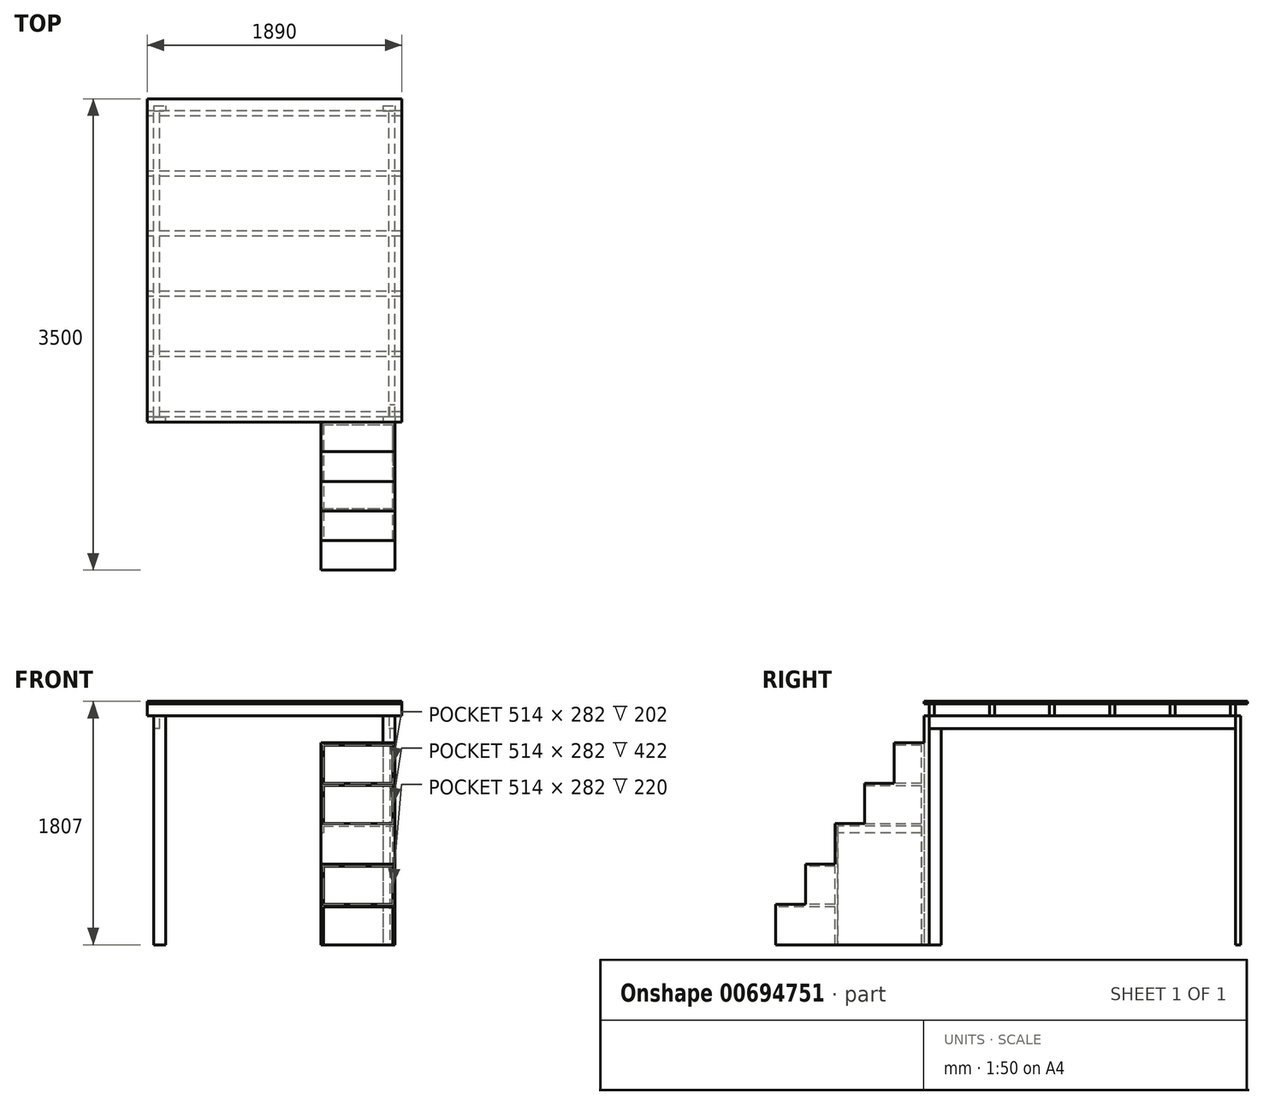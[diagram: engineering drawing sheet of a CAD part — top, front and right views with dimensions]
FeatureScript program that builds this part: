
annotation { "Feature Type Name" : "Feature", "Feature Type Description" : "" }
export const myFeature = defineFeature(function(context is Context, id is Id, definition is map)
    precondition{}
    {
        {
            var Q0;
            Q0=qCreatedBy(makeId("Top.planeOp"),FACE);
            var sketch = newSketch(context, id + "F0", { "sketchPlane" : qUnion([Q0])});
            skLineSegment(sketch, "E0.bottom", {"start": v(-895, 2350) * mm, "end": v(-806, 2350) * mm});
            skLineSegment(sketch, "E0.top", {"start": v(-895, 2312) * mm, "end": v(-806, 2312) * mm});
            skLineSegment(sketch, "E0.left", {"start": v(-895, 2350) * mm, "end": v(-895, 2312) * mm});
            skLineSegment(sketch, "E0.right", {"start": v(-806, 2350) * mm, "end": v(-806, 2312) * mm});
            skLineSegment(sketch, "E1.bottom", {"start": v(-895, 2312) * mm, "end": v(-857, 2312) * mm});
            skLineSegment(sketch, "E1.top", {"start": v(-895, 2223) * mm, "end": v(-857, 2223) * mm});
            skLineSegment(sketch, "E1.left", {"start": v(-895, 2312) * mm, "end": v(-895, 2223) * mm});
            skLineSegment(sketch, "E1.right", {"start": v(-857, 2312) * mm, "end": v(-857, 2223) * mm});
            skLineSegment(sketch, "E2.bottom", {"start": v(806, 2350) * mm, "end": v(895, 2350) * mm});
            skLineSegment(sketch, "E2.top", {"start": v(806, 2312) * mm, "end": v(895, 2312) * mm});
            skLineSegment(sketch, "E2.left", {"start": v(806, 2350) * mm, "end": v(806, 2312) * mm});
            skLineSegment(sketch, "E2.right", {"start": v(895, 2350) * mm, "end": v(895, 2312) * mm});
            skLineSegment(sketch, "E3.bottom", {"start": v(895, 2312) * mm, "end": v(857, 2312) * mm});
            skLineSegment(sketch, "E3.top", {"start": v(895, 2223) * mm, "end": v(857, 2223) * mm});
            skLineSegment(sketch, "E3.left", {"start": v(895, 2312) * mm, "end": v(895, 2223) * mm});
            skLineSegment(sketch, "E3.right", {"start": v(857, 2312) * mm, "end": v(857, 2223) * mm});
            skLineSegment(sketch, "E4.bottom", {"start": v(895, 38) * mm, "end": v(857, 38) * mm});
            skLineSegment(sketch, "E4.top", {"start": v(895, 127) * mm, "end": v(857, 127) * mm});
            skLineSegment(sketch, "E4.left", {"start": v(895, 38) * mm, "end": v(895, 127) * mm});
            skLineSegment(sketch, "E4.right", {"start": v(857, 38) * mm, "end": v(857, 127) * mm});
            skLineSegment(sketch, "E5.bottom", {"start": v(895, 38) * mm, "end": v(806, 38) * mm});
            skLineSegment(sketch, "E5.top", {"start": v(895, 0) * mm, "end": v(806, 0) * mm});
            skLineSegment(sketch, "E5.left", {"start": v(895, 38) * mm, "end": v(895, 0) * mm});
            skLineSegment(sketch, "E5.right", {"start": v(806, 38) * mm, "end": v(806, 0) * mm});
            skLineSegment(sketch, "E6.bottom", {"start": v(-895, 0) * mm, "end": v(-806, 0) * mm});
            skLineSegment(sketch, "E6.top", {"start": v(-895, 38) * mm, "end": v(-806, 38) * mm});
            skLineSegment(sketch, "E6.left", {"start": v(-895, 0) * mm, "end": v(-895, 38) * mm});
            skLineSegment(sketch, "E6.right", {"start": v(-806, 0) * mm, "end": v(-806, 38) * mm});
            skLineSegment(sketch, "E7.bottom", {"start": v(-895, 38) * mm, "end": v(-857, 38) * mm});
            skLineSegment(sketch, "E7.top", {"start": v(-895, 127) * mm, "end": v(-857, 127) * mm});
            skLineSegment(sketch, "E7.left", {"start": v(-895, 38) * mm, "end": v(-895, 127) * mm});
            skLineSegment(sketch, "E7.right", {"start": v(-857, 38) * mm, "end": v(-857, 127) * mm});
            skLineSegment(sketch, "E8", {"start": v(-806, 2350) * mm, "end": v(806, 2350) * mm, "construction": true});
            skLineSegment(sketch, "E9", {"start": v(895, 2223) * mm, "end": v(895, 127) * mm, "construction": true});
            skLineSegment(sketch, "E10", {"start": v(806, 0) * mm, "end": v(-806, 0) * mm, "construction": true});
            skLineSegment(sketch, "E11", {"start": v(-895, 127) * mm, "end": v(-895, 2223) * mm, "construction": true});
            skSolve(sketch);
        }
        {
            var Q0;
            Q0=makeQuery(id+"F0.imprint","IMPRINT",FACE,{"disambiguationData":[TD([[makeQuery(id+"F0.imprint","IMPRINT",EDGE,{"derivedFrom":sQuery(id+"F0.wireOp",EDGE,"E0.bottom")}),-1.0]])]});
            var Q1;
            Q1=makeQuery(id+"F0.imprint","IMPRINT",FACE,{"disambiguationData":[TD([[makeQuery(id+"F0.imprint","IMPRINT",EDGE,{"derivedFrom":sQuery(id+"F0.wireOp",EDGE,"E2.bottom")}),-1.0]])]});
            var Q2;
            Q2=makeQuery(id+"F0.imprint","IMPRINT",FACE,{"disambiguationData":[TD([[makeQuery(id+"F0.imprint","IMPRINT",EDGE,{"derivedFrom":sQuery(id+"F0.wireOp",EDGE,"E5.top")}),-1.0]])]});
            var Q3;
            Q3=makeQuery(id+"F0.imprint","IMPRINT",FACE,{"disambiguationData":[TD([[makeQuery(id+"F0.imprint","IMPRINT",EDGE,{"derivedFrom":sQuery(id+"F0.wireOp",EDGE,"E6.bottom")}),1.0]])]});
            extrude(context, id + "F1", {"entities" : qUnion([Q0, Q1, Q2, Q3]), "depth" : 1700 * mm, "offsetDistance" : 25 * mm});
        }
        {
            var Q0;
            Q0=makeQuery(id+"F0.imprint","IMPRINT",FACE,{"disambiguationData":[TD([[makeQuery(id+"F0.imprint","IMPRINT",EDGE,{"derivedFrom":sQuery(id+"F0.wireOp",EDGE,"E1.bottom")}),-1.0]])]});
            var Q1;
            Q1=makeQuery(id+"F0.imprint","IMPRINT",FACE,{"disambiguationData":[TD([[makeQuery(id+"F0.imprint","IMPRINT",EDGE,{"derivedFrom":sQuery(id+"F0.wireOp",EDGE,"E3.bottom")}),1.0]])]});
            var Q2;
            Q2=makeQuery(id+"F0.imprint","IMPRINT",FACE,{"disambiguationData":[TD([[makeQuery(id+"F0.imprint","IMPRINT",EDGE,{"derivedFrom":sQuery(id+"F0.wireOp",EDGE,"E4.top")}),1.0]])]});
            var Q3;
            Q3=makeQuery(id+"F0.imprint","IMPRINT",FACE,{"disambiguationData":[TD([[makeQuery(id+"F0.imprint","IMPRINT",EDGE,{"derivedFrom":sQuery(id+"F0.wireOp",EDGE,"E7.bottom")}),1.0]])]});
            extrude(context, id + "F2", {"entities" : qUnion([Q0, Q1, Q2, Q3]), "depth" : (1700 - 94) * mm, "offsetDistance" : 25 * mm});
        }
        {
            var Q0;
            Q0=makeQuery(id+"F1.opExtrude","SWEPT_FACE",FACE,{"disambiguationData":[OSD([sQuery(id+"F0.wireOp",EDGE,"E0.top"),sQuery(id+"F0.wireOp",EDGE,"E1.bottom")])]});
            var sketch = newSketch(context, id + "F3", { "sketchPlane" : qUnion([Q0])});
            skLineSegment(sketch, "E12.bottom", {"start": v(-895, 1700) * mm, "end": v(-851, 1700) * mm});
            skLineSegment(sketch, "E12.top", {"start": v(-895, 1606) * mm, "end": v(-851, 1606) * mm});
            skLineSegment(sketch, "E12.left", {"start": v(-895, 1700) * mm, "end": v(-895, 1606) * mm});
            skLineSegment(sketch, "E12.right", {"start": v(-851, 1700) * mm, "end": v(-851, 1606) * mm});
            skLineSegment(sketch, "E13.bottom", {"start": v(895, 1700) * mm, "end": v(851, 1700) * mm});
            skLineSegment(sketch, "E13.top", {"start": v(895, 1606) * mm, "end": v(851, 1606) * mm});
            skLineSegment(sketch, "E13.left", {"start": v(895, 1700) * mm, "end": v(895, 1606) * mm});
            skLineSegment(sketch, "E13.right", {"start": v(851, 1700) * mm, "end": v(851, 1606) * mm});
            skSolve(sketch);
        }
        {
            var Q0;
            Q0 = qSketchRegion(id + "F3", true);
            extrude(context, id + "F4", {"entities" : qUnion([Q0]), "endBound" : BoundingType.UP_TO_NEXT, "depth" : 25 * mm, "offsetDistance" : 25 * mm});
        }
        {
            var Q0;
            Q0=qCreatedBy(makeId("Right.planeOp"),FACE);
            var sketch = newSketch(context, id + "F5", { "sketchPlane" : qUnion([Q0])});
            skLineSegment(sketch, "E14.bottom", {"start": v(485.2, 1700) * mm, "end": v(523.2, 1700) * mm});
            skLineSegment(sketch, "E14.top", {"start": v(485.2, 1789) * mm, "end": v(523.2, 1789) * mm});
            skLineSegment(sketch, "E14.left", {"start": v(485.2, 1700) * mm, "end": v(485.2, 1789) * mm});
            skLineSegment(sketch, "E14.right", {"start": v(523.2, 1700) * mm, "end": v(523.2, 1789) * mm});
            skLineSegment(sketch, "E15.bottom", {"start": v(932.4, 1700) * mm, "end": v(970.4, 1700) * mm});
            skLineSegment(sketch, "E15.top", {"start": v(932.4, 1789) * mm, "end": v(970.4, 1789) * mm});
            skLineSegment(sketch, "E15.left", {"start": v(970.4, 1700) * mm, "end": v(970.4, 1789) * mm});
            skLineSegment(sketch, "E15.right", {"start": v(932.4, 1700) * mm, "end": v(932.4, 1789) * mm});
            skLineSegment(sketch, "E16.bottom", {"start": v(1379.6, 1789) * mm, "end": v(1417.6, 1789) * mm});
            skLineSegment(sketch, "E16.top", {"start": v(1379.6, 1700) * mm, "end": v(1417.6, 1700) * mm});
            skLineSegment(sketch, "E16.left", {"start": v(1417.6, 1789) * mm, "end": v(1417.6, 1700) * mm});
            skLineSegment(sketch, "E16.right", {"start": v(1379.6, 1789) * mm, "end": v(1379.6, 1700) * mm});
            skLineSegment(sketch, "E17.bottom", {"start": v(1826.8, 1789) * mm, "end": v(1864.8, 1789) * mm});
            skLineSegment(sketch, "E17.top", {"start": v(1826.8, 1700) * mm, "end": v(1864.8, 1700) * mm});
            skLineSegment(sketch, "E17.left", {"start": v(1826.8, 1789) * mm, "end": v(1826.8, 1700) * mm});
            skLineSegment(sketch, "E17.right", {"start": v(1864.8, 1789) * mm, "end": v(1864.8, 1700) * mm});
            skLineSegment(sketch, "E18", {"start": v(523.2, 1744.5) * mm, "end": v(932.4, 1744.5) * mm, "construction": true});
            skLineSegment(sketch, "E19", {"start": v(970.4, 1744.5) * mm, "end": v(1379.6, 1744.5) * mm, "construction": true});
            skLineSegment(sketch, "E20", {"start": v(1417.6, 1744.5) * mm, "end": v(1826.8, 1744.5) * mm, "construction": true});
            skLineSegment(sketch, "E21.bottom", {"start": v(38, 1700) * mm, "end": v(76, 1700) * mm});
            skLineSegment(sketch, "E21.top", {"start": v(38, 1789) * mm, "end": v(76, 1789) * mm});
            skLineSegment(sketch, "E21.left", {"start": v(38, 1700) * mm, "end": v(38, 1789) * mm});
            skLineSegment(sketch, "E21.right", {"start": v(76, 1700) * mm, "end": v(76, 1789) * mm});
            skLineSegment(sketch, "E22.bottom", {"start": v(2274, 1789) * mm, "end": v(2312, 1789) * mm});
            skLineSegment(sketch, "E22.top", {"start": v(2274, 1700) * mm, "end": v(2312, 1700) * mm});
            skLineSegment(sketch, "E22.left", {"start": v(2274, 1789) * mm, "end": v(2274, 1700) * mm});
            skLineSegment(sketch, "E22.right", {"start": v(2312, 1789) * mm, "end": v(2312, 1700) * mm});
            skLineSegment(sketch, "E23", {"start": v(2274, 1744.5) * mm, "end": v(1864.8, 1744.5) * mm, "construction": true});
            skLineSegment(sketch, "E24", {"start": v(485.2, 1744.5) * mm, "end": v(76, 1744.5) * mm, "construction": true});
            skSolve(sketch);
        }
        {
            var Q0;
            Q0 = qSketchRegion(id + "F5", true);
            extrude(context, id + "F6", {"entities" : qUnion([Q0]), "depth" : 945 * mm, "offsetDistance" : 25 * mm, "hasSecondDirection" : true, "secondDirectionOppositeDirection" : true, "secondDirectionDepth" : 945 * mm});
        }
        {
            var Q0;
            Q0=makeQuery(id+"F6.opExtrude","SWEPT_FACE",FACE,{"disambiguationData":[OSD([sQuery(id+"F5.wireOp",EDGE,"E14.top")])]});
            var sketch = newSketch(context, id + "F7", { "sketchPlane" : qUnion([Q0])});
            skLineSegment(sketch, "E25.bottom", {"start": v(945, 0) * mm, "end": v(-945, 0) * mm});
            skLineSegment(sketch, "E25.top", {"start": v(945, 2400) * mm, "end": v(-945, 2400) * mm});
            skLineSegment(sketch, "E25.left", {"start": v(945, 0) * mm, "end": v(945, 2400) * mm});
            skLineSegment(sketch, "E25.right", {"start": v(-945, 0) * mm, "end": v(-945, 2400) * mm});
            skSolve(sketch);
        }
        {
            var Q0;
            Q0 = qSketchRegion(id + "F7", true);
            extrude(context, id + "F8", {"entities" : qUnion([Q0]), "depth" : 18 * mm, "offsetDistance" : 25 * mm});
        }
        {
            var Q0;
            Q0=makeQuery(id+"F2.opExtrude","SWEPT_FACE",FACE,{"disambiguationData":[OSD([sQuery(id+"F0.wireOp",EDGE,"E4.left")])]});
            var sketch = newSketch(context, id + "F9", { "sketchPlane" : qUnion([Q0])});
            skLineSegment(sketch, "E26.top", {"start": v(0, 1500) * mm, "end": v(-220, 1500) * mm});
            skLineSegment(sketch, "E26.left", {"start": v(0, 0) * mm, "end": v(0, 1182) * mm});
            skLineSegment(sketch, "E26.right", {"start": v(-220, 1200) * mm, "end": v(-220, 1500) * mm});
            skLineSegment(sketch, "E27.top", {"start": v(-220, 1200) * mm, "end": v(-440, 1200) * mm});
            skLineSegment(sketch, "E27.right", {"start": v(-440, 900) * mm, "end": v(-440, 1200) * mm});
            skLineSegment(sketch, "E28.top", {"start": v(-440, 900) * mm, "end": v(-660, 900) * mm});
            skLineSegment(sketch, "E28.right", {"start": v(-660, 600) * mm, "end": v(-660, 900) * mm});
            skLineSegment(sketch, "E29.top", {"start": v(-660, 600) * mm, "end": v(-880, 600) * mm});
            skLineSegment(sketch, "E29.right", {"start": v(-880, 300) * mm, "end": v(-880, 600) * mm});
            skLineSegment(sketch, "E30.top", {"start": v(-880, 300) * mm, "end": v(-1100, 300) * mm});
            skLineSegment(sketch, "E30.right", {"start": v(-1100, 0) * mm, "end": v(-1100, 300) * mm});
            skLineSegment(sketch, "E31", {"start": v(-1100, 0) * mm, "end": v(0, 0) * mm});
            skLineSegment(sketch, "E32.0", {"start": v(-1082, 0) * mm, "end": v(-1082, 282) * mm});
            skLineSegment(sketch, "E32.1", {"start": v(-202, 1182) * mm, "end": v(-422, 1182) * mm});
            skLineSegment(sketch, "E32.2", {"start": v(-202, 1200) * mm, "end": v(-202, 1482) * mm});
            skLineSegment(sketch, "E32.3", {"start": v(-18, 1482) * mm, "end": v(-202, 1482) * mm});
            skLineSegment(sketch, "E32.4", {"start": v(-18, 0) * mm, "end": v(-18, 1482) * mm});
            skLineSegment(sketch, "E32.5", {"start": v(-422, 900) * mm, "end": v(-422, 1182) * mm});
            skLineSegment(sketch, "E32.6", {"start": v(-422, 882) * mm, "end": v(-642, 882) * mm});
            skLineSegment(sketch, "E32.7", {"start": v(-642, 582) * mm, "end": v(-642, 882) * mm});
            skLineSegment(sketch, "E32.8", {"start": v(-660, 582) * mm, "end": v(-862, 582) * mm});
            skLineSegment(sketch, "E32.9", {"start": v(-862, 300) * mm, "end": v(-862, 582) * mm});
            skLineSegment(sketch, "E32.10", {"start": v(-862, 282) * mm, "end": v(-1082, 282) * mm});
            skLineSegment(sketch, "E33", {"start": v(-1400, 0) * mm, "end": v(-1400, 1597.73) * mm});
            skLineSegment(sketch, "E34.top", {"start": v(-660, 0) * mm, "end": v(-642, 0) * mm});
            skLineSegment(sketch, "E34.left", {"start": v(-660, 600) * mm, "end": v(-660, 0) * mm});
            skLineSegment(sketch, "E34.right", {"start": v(-642, 582) * mm, "end": v(-642, 0) * mm});
            skLineSegment(sketch, "E35.bottom", {"start": v(-220, 1200) * mm, "end": v(-18, 1200) * mm});
            skLineSegment(sketch, "E35.top", {"start": v(-202, 1182) * mm, "end": v(-18, 1182) * mm});
            skLineSegment(sketch, "E35.right", {"start": v(0, 1200) * mm, "end": v(0, 1182) * mm});
            skLineSegment(sketch, "E36.trimOffspring", {"start": v(0, 1200) * mm, "end": v(0, 1500) * mm});
            skLineSegment(sketch, "E37.bottom", {"start": v(-422, 882) * mm, "end": v(-18, 882) * mm});
            skLineSegment(sketch, "E37.top", {"start": v(-422, 900) * mm, "end": v(-18, 900) * mm});
            skLineSegment(sketch, "E37.right", {"start": v(-18, 882) * mm, "end": v(-18, 900) * mm});
            skLineSegment(sketch, "E38", {"start": v(-440, 900) * mm, "end": v(-422, 900) * mm});
            skLineSegment(sketch, "E39.bottom", {"start": v(-862, 282) * mm, "end": v(-660, 282) * mm});
            skLineSegment(sketch, "E39.top", {"start": v(-862, 300) * mm, "end": v(-660, 300) * mm});
            skLineSegment(sketch, "E39.right", {"start": v(-660, 282) * mm, "end": v(-660, 300) * mm});
            skLineSegment(sketch, "E40", {"start": v(-880, 300) * mm, "end": v(-862, 300) * mm});
            skLineSegment(sketch, "E41", {"start": v(-202, 1482) * mm, "end": v(-220, 1482) * mm});
            skLineSegment(sketch, "E42", {"start": v(-422, 1182) * mm, "end": v(-440, 1182) * mm});
            skLineSegment(sketch, "E43", {"start": v(-862, 582) * mm, "end": v(-880, 582) * mm});
            skLineSegment(sketch, "E44", {"start": v(-1082, 282) * mm, "end": v(-1100, 282) * mm});
            skSolve(sketch);
        }
        {
            var Q0;
            {var subQ2=sQuery(id+"F9.wireOp",EDGE,"E29.top");Q0=makeQuery(id+"F9.imprint","IMPRINT",FACE,{"disambiguationData":[TD([[makeQuery(id+"F9.imprint","IMPRINT",EDGE,{"derivedFrom":subQ2}),1.0]])]});}
            var Q1;
            {var subQ4=sQuery(id+"F9.wireOp",EDGE,"E27.top");Q1=makeQuery(id+"F9.imprint","IMPRINT",FACE,{"disambiguationData":[TD([[makeQuery(id+"F9.imprint","IMPRINT",EDGE,{"derivedFrom":subQ4}),1.0]])]});}
            var Q2;
            Q2=makeQuery(id+"F9.imprint","IMPRINT",FACE,{"disambiguationData":[TD([[makeQuery(id+"F9.imprint","IMPRINT",EDGE,{"derivedFrom":sQuery(id+"F9.wireOp",EDGE,"E30.top")}),1.0]])]});
            var Q3;
            Q3=makeQuery(id+"F9.imprint","IMPRINT",FACE,{"disambiguationData":[TD([[makeQuery(id+"F9.imprint","IMPRINT",EDGE,{"derivedFrom":sQuery(id+"F9.wireOp",EDGE,"E26.top")}),1.0]])]});
            var Q4;
            Q4=makeQuery(id+"F9.imprint","IMPRINT",FACE,{"disambiguationData":[TD([[makeQuery(id+"F9.imprint","IMPRINT",EDGE,{"derivedFrom":sQuery(id+"F9.wireOp",EDGE,"E28.top")}),1.0]])]});
            extrude(context, id + "F10", {"entities" : qUnion([Q0, Q1, Q2, Q3, Q4]), "oppositeDirection" : true, "depth" : 550 * mm, "offsetDistance" : 25 * mm});
        }
        {
            var Q0;
            Q0=makeQuery(id+"F10.opExtrude","CAP_FACE",FACE,{"disambiguationData":[OSD([sQuery(id+"F9.wireOp",EDGE,"E26.top"),sQuery(id+"F9.wireOp",EDGE,"E26.left"),sQuery(id+"F9.wireOp",EDGE,"E26.right"),sQuery(id+"F9.wireOp",EDGE,"E27.top"),sQuery(id+"F9.wireOp",EDGE,"E27.right"),sQuery(id+"F9.wireOp",EDGE,"E28.top"),sQuery(id+"F9.wireOp",EDGE,"E28.right"),sQuery(id+"F9.wireOp",EDGE,"E29.top"),sQuery(id+"F9.wireOp",EDGE,"E29.right"),sQuery(id+"F9.wireOp",EDGE,"E30.top"),sQuery(id+"F9.wireOp",EDGE,"E30.right"),sQuery(id+"F9.wireOp",EDGE,"E31"),sQuery(id+"F9.wireOp",EDGE,"E32.0"),sQuery(id+"F9.wireOp",EDGE,"E32.1"),sQuery(id+"F9.wireOp",EDGE,"E32.2"),sQuery(id+"F9.wireOp",EDGE,"E32.3"),sQuery(id+"F9.wireOp",EDGE,"E32.4"),sQuery(id+"F9.wireOp",EDGE,"E32.5"),sQuery(id+"F9.wireOp",EDGE,"E32.6"),sQuery(id+"F9.wireOp",EDGE,"E32.7"),sQuery(id+"F9.wireOp",EDGE,"E32.8"),sQuery(id+"F9.wireOp",EDGE,"E32.9"),sQuery(id+"F9.wireOp",EDGE,"E32.10"),sQuery(id+"F9.wireOp",EDGE,"E34.top"),sQuery(id+"F9.wireOp",EDGE,"E34.left"),sQuery(id+"F9.wireOp",EDGE,"E34.right"),sQuery(id+"F9.wireOp",EDGE,"E35.bottom"),sQuery(id+"F9.wireOp",EDGE,"E35.top"),sQuery(id+"F9.wireOp",EDGE,"E35.right"),sQuery(id+"F9.wireOp",EDGE,"E36.trimOffspring"),sQuery(id+"F9.wireOp",EDGE,"E37.bottom"),sQuery(id+"F9.wireOp",EDGE,"E37.top"),sQuery(id+"F9.wireOp",EDGE,"E39.bottom"),sQuery(id+"F9.wireOp",EDGE,"E39.top")])],"isStart":true});
            var sketch = newSketch(context, id + "F11", { "sketchPlane" : qUnion([Q0])});
            skLineSegment(sketch, "E45", {"start": v(0, 1500) * mm, "end": v(-220, 1500) * mm});
            skLineSegment(sketch, "E46", {"start": v(-220, 1500) * mm, "end": v(-220, 1200) * mm});
            skLineSegment(sketch, "E47", {"start": v(-220, 1200) * mm, "end": v(-440, 1200) * mm});
            skLineSegment(sketch, "E48", {"start": v(-440, 1200) * mm, "end": v(-440, 900) * mm});
            skLineSegment(sketch, "E49", {"start": v(-440, 900) * mm, "end": v(-660, 900) * mm});
            skLineSegment(sketch, "E50", {"start": v(-660, 900) * mm, "end": v(-660, 600) * mm});
            skLineSegment(sketch, "E51", {"start": v(-660, 600) * mm, "end": v(-880, 600) * mm});
            skLineSegment(sketch, "E52", {"start": v(-880, 600) * mm, "end": v(-880, 300) * mm});
            skLineSegment(sketch, "E53", {"start": v(-880, 300) * mm, "end": v(-1100, 300) * mm});
            skLineSegment(sketch, "E54", {"start": v(-1100, 300) * mm, "end": v(-1100, 0) * mm});
            skLineSegment(sketch, "E55", {"start": v(-1100, 0) * mm, "end": v(0, 0) * mm});
            skLineSegment(sketch, "E56", {"start": v(0, 0) * mm, "end": v(0, 1500) * mm});
            skSolve(sketch);
        }
        {
            var Q0;
            Q0 = qSketchRegion(id + "F11", true);
            extrude(context, id + "F12", {"entities" : qUnion([Q0]), "operationType" : NewBodyOperationType.ADD, "oppositeDirection" : true, "depth" : 18 * mm, "offsetDistance" : 25 * mm});
        }
        {
            var Q0;
            Q0=makeQuery(id+"F10.opExtrude","CAP_FACE",FACE,{"disambiguationData":[OSD([sQuery(id+"F9.wireOp",EDGE,"E26.top"),sQuery(id+"F9.wireOp",EDGE,"E26.left"),sQuery(id+"F9.wireOp",EDGE,"E26.right"),sQuery(id+"F9.wireOp",EDGE,"E27.top"),sQuery(id+"F9.wireOp",EDGE,"E27.right"),sQuery(id+"F9.wireOp",EDGE,"E28.top"),sQuery(id+"F9.wireOp",EDGE,"E28.right"),sQuery(id+"F9.wireOp",EDGE,"E29.top"),sQuery(id+"F9.wireOp",EDGE,"E29.right"),sQuery(id+"F9.wireOp",EDGE,"E30.top"),sQuery(id+"F9.wireOp",EDGE,"E30.right"),sQuery(id+"F9.wireOp",EDGE,"E31"),sQuery(id+"F9.wireOp",EDGE,"E32.1"),sQuery(id+"F9.wireOp",EDGE,"E32.3"),sQuery(id+"F9.wireOp",EDGE,"E32.4"),sQuery(id+"F9.wireOp",EDGE,"E32.6"),sQuery(id+"F9.wireOp",EDGE,"E32.7"),sQuery(id+"F9.wireOp",EDGE,"E32.8"),sQuery(id+"F9.wireOp",EDGE,"E32.10"),sQuery(id+"F9.wireOp",EDGE,"E34.top"),sQuery(id+"F9.wireOp",EDGE,"E34.left"),sQuery(id+"F9.wireOp",EDGE,"E34.right"),sQuery(id+"F9.wireOp",EDGE,"E35.bottom"),sQuery(id+"F9.wireOp",EDGE,"E35.top"),sQuery(id+"F9.wireOp",EDGE,"E35.right"),sQuery(id+"F9.wireOp",EDGE,"E36.trimOffspring"),sQuery(id+"F9.wireOp",EDGE,"E37.bottom"),sQuery(id+"F9.wireOp",EDGE,"E37.top"),sQuery(id+"F9.wireOp",EDGE,"E38"),sQuery(id+"F9.wireOp",EDGE,"E39.bottom"),sQuery(id+"F9.wireOp",EDGE,"E39.top"),sQuery(id+"F9.wireOp",EDGE,"E40"),sQuery(id+"F9.wireOp",EDGE,"E41"),sQuery(id+"F9.wireOp",EDGE,"E42"),sQuery(id+"F9.wireOp",EDGE,"E43"),sQuery(id+"F9.wireOp",EDGE,"E44")])],"isStart":false});
            var sketch = newSketch(context, id + "F13", { "sketchPlane" : qUnion([Q0])});
            skLineSegment(sketch, "E57", {"start": v(0, 1500) * mm, "end": v(220, 1500) * mm});
            skLineSegment(sketch, "E58", {"start": v(220, 1500) * mm, "end": v(220, 1200) * mm});
            skLineSegment(sketch, "E59", {"start": v(220, 1200) * mm, "end": v(440, 1200) * mm});
            skLineSegment(sketch, "E60", {"start": v(440, 1200) * mm, "end": v(440, 900) * mm});
            skLineSegment(sketch, "E61", {"start": v(440, 900) * mm, "end": v(0, 900) * mm});
            skLineSegment(sketch, "E62", {"start": v(0, 900) * mm, "end": v(0, 1500) * mm});
            skLineSegment(sketch, "E63", {"start": v(660, 600) * mm, "end": v(880, 600) * mm});
            skLineSegment(sketch, "E64", {"start": v(880, 600) * mm, "end": v(880, 300) * mm});
            skLineSegment(sketch, "E65", {"start": v(880, 300) * mm, "end": v(1100, 300) * mm});
            skLineSegment(sketch, "E66", {"start": v(1100, 300) * mm, "end": v(1100, 0) * mm});
            skLineSegment(sketch, "E67", {"start": v(1100, 0) * mm, "end": v(660, 0) * mm});
            skLineSegment(sketch, "E68", {"start": v(660, 0) * mm, "end": v(660, 600) * mm});
            skLineSegment(sketch, "E69.bottom", {"start": v(18, 882) * mm, "end": v(642, 882) * mm});
            skLineSegment(sketch, "E69.top", {"start": v(18, 832) * mm, "end": v(642, 832) * mm});
            skLineSegment(sketch, "E69.left", {"start": v(18, 882) * mm, "end": v(18, 832) * mm});
            skLineSegment(sketch, "E69.right", {"start": v(642, 882) * mm, "end": v(642, 832) * mm});
            skSolve(sketch);
        }
        {
            var Q0;
            Q0 = qSketchRegion(id + "F13", true);
            extrude(context, id + "F14", {"entities" : qUnion([Q0]), "operationType" : NewBodyOperationType.ADD, "oppositeDirection" : true, "depth" : 18 * mm, "offsetDistance" : 25 * mm});
        }
    });
